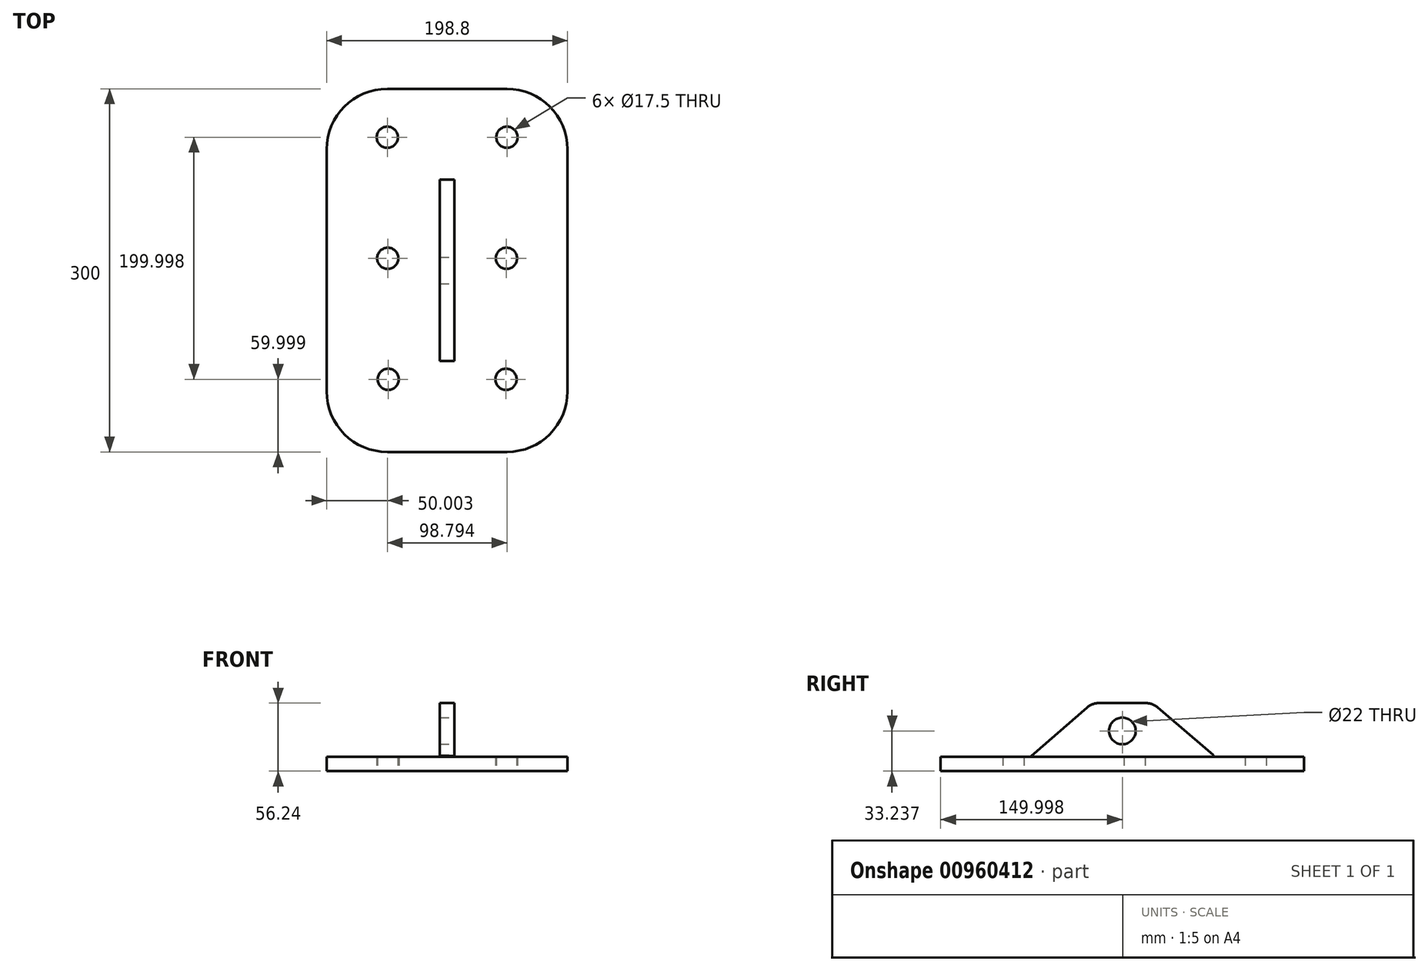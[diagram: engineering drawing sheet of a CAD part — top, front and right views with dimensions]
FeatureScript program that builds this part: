
annotation { "Feature Type Name" : "Feature", "Feature Type Description" : "" }
export const myFeature = defineFeature(function(context is Context, id is Id, definition is map)
    precondition{}
    {
        {
            var Q0;
            Q0=qCreatedBy(makeId("Top.planeOp"),FACE);
            var sketch = newSketch(context, id + "F0", { "sketchPlane" : qUnion([Q0])});
            skLineSegment(sketch, "E0.bottom", {"start": v(-99.4, 162.6) * mm, "end": v(0.6, 162.6) * mm});
            skLineSegment(sketch, "E0.top", {"start": v(-99.4, -137.4) * mm, "end": v(0.6, -137.4) * mm});
            skLineSegment(sketch, "E0.left", {"start": v(-99.4, 162.6) * mm, "end": v(-99.4, -137.4) * mm});
            skLineSegment(sketch, "E0.right", {"start": v(0.6, 162.6) * mm, "end": v(0.6, -137.4) * mm});
            skSolve(sketch);
        }
        {
            var Q0;
            Q0=makeQuery(id+"F0.imprint","IMPRINT",FACE,{"disambiguationData":[TD([[makeQuery(id+"F0.imprint","IMPRINT",EDGE,{"derivedFrom":sQuery(id+"F0.wireOp",EDGE,"E0.bottom")}),-1.0]])]});
            var sketch = newSketch(context, id + "F1", { "sketchPlane" : qUnion([Q0])});
            skLineSegment(sketch, "E1", {"start": v(0, 203.4) * mm, "end": v(0, -174.16) * mm});
            skCircle(sketch, "E2", {"center": v(-49.4, 122.6) * mm, "radius": 8.75 * mm});
            skCircle(sketch, "E3.1.0.0", {"center": v(-49, 22.6) * mm, "radius": 8.75 * mm});
            skCircle(sketch, "E3.2.0.0", {"center": v(-48.62, -77.4) * mm, "radius": 8.75 * mm});
            skLineSegment(sketch, "E3.direction1", {"start": v(-49.4, 122.6) * mm, "end": v(-49, 22.6) * mm, "construction": true});
            skSolve(sketch);
        }
        {
            var Q0;
            {var subQ5=makeQuery(id+"F0.imprint","IMPRINT",EDGE,{"derivedFrom":sQuery(id+"F0.wireOp",EDGE,"E0.left")});Q0=makeQuery(id+"F1.imprint","IMPRINT",FACE,{"disambiguationData":[TD([[makeQuery(id+"F1.imprint","IMPRINT",EDGE,{"derivedFrom":subQ5}),1.0]])]});}
            extrude(context, id + "F2", {"entities" : qUnion([Q0]), "depth" : 12 * mm, "offsetDistance" : 25 * mm});
        }
        {
            var Q0;
            Q0=qCreatedBy(makeId("Right.planeOp"),FACE);
            var sketch = newSketch(context, id + "F3", { "sketchPlane" : qUnion([Q0])});
            skLineSegment(sketch, "E4", {"start": v(-62.4, 0) * mm, "end": v(-62.4, 12.5) * mm});
            skLineSegment(sketch, "E5", {"start": v(-62.4, 12.5) * mm, "end": v(-12.4, 56.24) * mm});
            skLineSegment(sketch, "E6", {"start": v(-12.4, 56.24) * mm, "end": v(37.6, 56.24) * mm});
            skLineSegment(sketch, "E7", {"start": v(37.6, 56.24) * mm, "end": v(87.6, 13.48) * mm});
            skLineSegment(sketch, "E8", {"start": v(87.6, 13.48) * mm, "end": v(87.6, 0) * mm});
            skLineSegment(sketch, "E9", {"start": v(87.6, 0) * mm, "end": v(-62.4, 0) * mm});
            skSolve(sketch);
        }
        {
            var Q0;
            Q0=makeQuery(id+"F3.imprint","IMPRINT",FACE,{"disambiguationData":[TD([[makeQuery(id+"F3.imprint","IMPRINT",EDGE,{"derivedFrom":sQuery(id+"F3.wireOp",EDGE,"E4")}),-1.0]])]});
            extrude(context, id + "F4", {"entities" : qUnion([Q0]), "operationType" : NewBodyOperationType.ADD, "oppositeDirection" : true, "depth" : 6 * mm, "offsetDistance" : 25 * mm});
        }
        {
            var Q0;
            Q0=qCreatedBy(makeId("Right.planeOp"),FACE);
            var sketch = newSketch(context, id + "F5", { "sketchPlane" : qUnion([Q0])});
            skCircle(sketch, "E10", {"center": v(12.6, 33.24) * mm, "radius": 13 * mm});
            skSolve(sketch);
        }
        {
            var Q0;
            Q0=sQuery(id+"F5.wireOp",VERTEX,"E10.center");
            var Q1;
            Q1=makeQuery(id+"F2.opExtrude","SWEPT_BODY",BODY,{"disambiguationData":[OSD([sQuery(id+"F0.wireOp",EDGE,"E0.bottom"),sQuery(id+"F0.wireOp",EDGE,"E0.top"),sQuery(id+"F0.wireOp",EDGE,"E0.left"),sQuery(id+"F1.wireOp",EDGE,"E1"),sQuery(id+"F1.wireOp",EDGE,"E2"),sQuery(id+"F1.wireOp",EDGE,"E3.1.0.0"),sQuery(id+"F1.wireOp",EDGE,"E3.2.0.0"),sQuery(id+"F1.wireOp",EDGE,"E3.3.0.0")])]});
            hole(context, id + "F6", {"style" : HoleStyle.SIMPLE, "endStyle" : HoleEndStyle.THROUGH, "standardTappedOrClearance" : lookupTablePath({ "fit" : "Normal", "standard" : "ISO", "size" : "M20", "type" : "Clearance" }), "standardBlindInLast" : lookupTablePath({ "fit" : "Normal", "standard" : "ISO", "engagement" : "75%", "pitch" : "2.5 mm", "size" : "M20", "type" : "Clearance & tapped" }), "holeDiameter" : 22 * mm, "majorDiameter" : 20 * mm, "isTappedThrough" : true, "tappedDepth" : 14.75 * mm, "tapClearance" : 3, "locations" : qUnion([Q0]), "scope" : qUnion([Q1])});
        }
        {
            var Q0;
            Q0=makeQuery(id+"F2.opExtrude","SWEPT_BODY",BODY,{"disambiguationData":[OSD([sQuery(id+"F0.wireOp",EDGE,"E0.bottom"),sQuery(id+"F0.wireOp",EDGE,"E0.top"),sQuery(id+"F0.wireOp",EDGE,"E0.left"),sQuery(id+"F1.wireOp",EDGE,"E1"),sQuery(id+"F1.wireOp",EDGE,"E2"),sQuery(id+"F1.wireOp",EDGE,"E3.1.0.0"),sQuery(id+"F1.wireOp",EDGE,"E3.2.0.0"),sQuery(id+"F1.wireOp",EDGE,"E3.3.0.0")])]});
            var Q1;
            Q1=makeQuery(id+"F4.boolean.opBoolean","MERGE",FACE,{"derivedFrom":[makeQuery(id+"F2.opExtrude","SWEPT_FACE",FACE,{"disambiguationData":[OSD([sQuery(id+"F1.wireOp",EDGE,"E1")])]}),makeQuery(id+"F4.opExtrude","CAP_FACE",FACE,{"disambiguationData":[OSD([sQuery(id+"F3.wireOp",EDGE,"E4"),sQuery(id+"F3.wireOp",EDGE,"E5"),sQuery(id+"F3.wireOp",EDGE,"E6"),sQuery(id+"F3.wireOp",EDGE,"E7"),sQuery(id+"F3.wireOp",EDGE,"E8"),sQuery(id+"F3.wireOp",EDGE,"E9")])],"isStart":true})]});
            mirror(context, id + "F7", {"operationType" : NewBodyOperationType.ADD, "entities" : qUnion([Q0]), "mirrorPlane" : qUnion([Q1])});
        }
        {
            var Q0;
            Q0=makeQuery(id+"F2.opExtrude","SWEPT_EDGE",EDGE,{"disambiguationData":[OSD([sQuery(id+"F0.wireOp",EDGE,"E0.bottom"),sQuery(id+"F0.wireOp",EDGE,"E0.left")])]});
            var Q1;
            Q1=makeQuery(id+"F7.opPattern","COPY",EDGE,{"derivedFrom":makeQuery(id+"F2.opExtrude","SWEPT_EDGE",EDGE,{"disambiguationData":[OSD([sQuery(id+"F0.wireOp",EDGE,"E0.bottom"),sQuery(id+"F0.wireOp",EDGE,"E0.left")])]}),"instanceName":"1"});
            var Q2;
            Q2=makeQuery(id+"F7.opPattern","COPY",EDGE,{"derivedFrom":makeQuery(id+"F2.opExtrude","SWEPT_EDGE",EDGE,{"disambiguationData":[OSD([sQuery(id+"F0.wireOp",EDGE,"E0.top"),sQuery(id+"F0.wireOp",EDGE,"E0.left")])]}),"instanceName":"1"});
            var Q3;
            Q3=makeQuery(id+"F2.opExtrude","SWEPT_EDGE",EDGE,{"disambiguationData":[OSD([sQuery(id+"F0.wireOp",EDGE,"E0.top"),sQuery(id+"F0.wireOp",EDGE,"E0.left")])]});
            fillet(context, id + "F8", {"entities" : qUnion([Q0, Q1, Q2, Q3]), "radius" : 50 * mm, "tangentPropagation" : true, "allowEdgeOverflow" : false});
        }
        {
            var Q0;
            {var subQ0=makeQuery(id+"F4.opExtrude","SWEPT_EDGE",EDGE,{"disambiguationData":[OSD([sQuery(id+"F3.wireOp",EDGE,"E6"),sQuery(id+"F3.wireOp",EDGE,"E7")])]});Q0=makeQuery(id+"F7.boolean.opBoolean","MERGE",EDGE,{"derivedFrom":[subQ0,makeQuery(id+"F7.opPattern","COPY",EDGE,{"derivedFrom":subQ0,"instanceName":"1"})]});}
            var Q1;
            {var subQ0=makeQuery(id+"F4.opExtrude","SWEPT_EDGE",EDGE,{"disambiguationData":[OSD([sQuery(id+"F3.wireOp",EDGE,"E5"),sQuery(id+"F3.wireOp",EDGE,"E6")])]});Q1=makeQuery(id+"F7.boolean.opBoolean","MERGE",EDGE,{"derivedFrom":[subQ0,makeQuery(id+"F7.opPattern","COPY",EDGE,{"derivedFrom":subQ0,"instanceName":"1"})]});}
            fillet(context, id + "F9", {"entities" : qUnion([Q0, Q1]), "radius" : 15 * mm, "tangentPropagation" : true, "allowEdgeOverflow" : false});
        }
    });
